# Revit family: Railing_Hatch-Defender-II_BlueWater
name_source: partatom
category: Railings
units: mm (PartAtom-declared; Revit-internal decimal feet)

## family parameters
Always vertical = Yes
Cut with Voids When Loaded = No
Shared = No
Work Plane-Based = No

## types (5) — shared parameters
Building Codes = http://bluewater-mfg.com
Construction Details = https://www.arcat.com
Description = Hatch Guardrail
Front Clearance = 15 1/2"
Green Building-LEED = https://www.arcat.com
Hardware Material = Steel - Galvanized - BlueWater
Height = 42"
Installation-Fabrication = https://www.arcat.com
Keynote = 05 52 00
Manufacturer = BlueWater
Manufacturer Website = http://bluewater-mfg.com
Product Data = https://www.arcat.com
Rear Clearance = 9 1/2"
Revision = R1_2018-05
Sales Information = http://bluewater-mfg.com
Side Clearance = 6"
Specification = https://www.arcat.com
URL = http://bluewater-mfg.com

## per-type parameters (varying)
| type | Hatch Opening Depth | Hatch Opening Width | Hatch Outside Depth | Hatch Outside Width | Model |
| 30-36 x 30-36 | 30" | 30" | 32" | 32" | Hatch Defender II 30-36 x 30-36 |
| 30-36 x 42 | 42" | 30" | 44" | 32" | Hatch Defender II 30-36 x 42 |
| 30-36 x 54 | 54" | 30" | 56" | 32" | Hatch Defender II 30-36 x 54 |
| 30-36 x 96 | 96" | 30" | 98" | 32" | Hatch Defender II 30-36 x 96 |
| 48 x 48 | 48" | 48" | 50" | 50" | Hatch Defender II 48 x 48 |

## geometry (parser evidence)
native form markers: Blend x36, Sweep x6
no freeform markers — native parametric forms only
